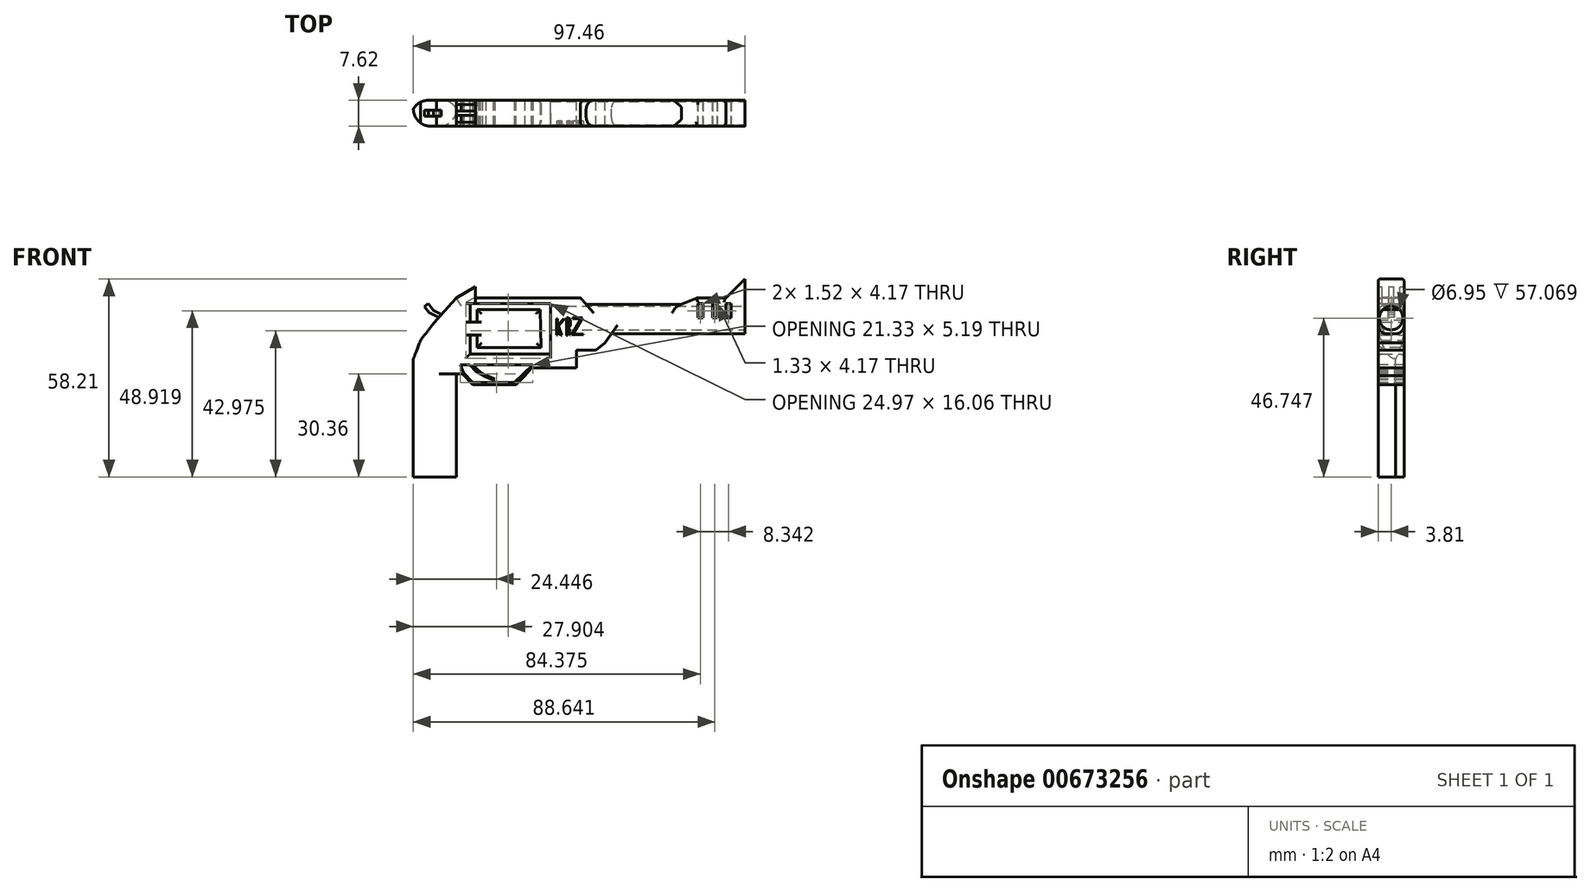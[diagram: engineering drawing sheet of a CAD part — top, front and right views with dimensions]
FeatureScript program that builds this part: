
annotation { "Feature Type Name" : "Feature", "Feature Type Description" : "" }
export const myFeature = defineFeature(function(context is Context, id is Id, definition is map)
    precondition{}
    {
        {
            var Q0;
            Q0=qCreatedBy(makeId("Front.planeOp"),FACE);
            var sketch = newSketch(context, id + "F0", { "sketchPlane" : qUnion([Q0])});
            skLineSegment(sketch, "E0", {"start": v(-48.06, -27.2) * mm, "end": v(-48.06, 3.13) * mm});
            skLineSegment(sketch, "E1", {"start": v(-48.06, 3.13) * mm, "end": v(-46.36, 3.13) * mm});
            skLineSegment(sketch, "E2", {"start": v(-46.36, 3.13) * mm, "end": v(-43.32, 0) * mm});
            skLineSegment(sketch, "E3", {"start": v(-43.32, 0) * mm, "end": v(-38.77, 0) * mm});
            skLineSegment(sketch, "E4", {"start": v(-38.77, 0) * mm, "end": v(-30.62, 0) * mm});
            skLineSegment(sketch, "E5", {"start": v(-30.62, 0) * mm, "end": v(-27.97, 2.56) * mm});
            skLineSegment(sketch, "E6", {"start": v(-27.97, 2.56) * mm, "end": v(-26.07, 4.83) * mm});
            skLineSegment(sketch, "E7", {"start": v(-26.07, 4.83) * mm, "end": v(-12.8, 4.83) * mm});
            skLineSegment(sketch, "E8", {"start": v(-12.8, 4.83) * mm, "end": v(-12.8, 10.14) * mm});
            skLineSegment(sketch, "E9", {"start": v(-12.8, 10.14) * mm, "end": v(-10.52, 10.14) * mm});
            skLineSegment(sketch, "E10", {"start": v(-10.52, 10.14) * mm, "end": v(-7.1, 10.14) * mm});
            skLineSegment(sketch, "E11", {"start": v(-7.1, 10.14) * mm, "end": v(-4.46, 12.23) * mm});
            skLineSegment(sketch, "E12", {"start": v(-4.46, 12.23) * mm, "end": v(-2.56, 14.88) * mm});
            skLineSegment(sketch, "E13", {"start": v(-2.56, 14.88) * mm, "end": v(4.83, 14.88) * mm});
            skLineSegment(sketch, "E14", {"start": v(4.83, 14.88) * mm, "end": v(14.88, 14.88) * mm});
            skLineSegment(sketch, "E15", {"start": v(14.88, 14.88) * mm, "end": v(23.8, 14.88) * mm});
            skLineSegment(sketch, "E16", {"start": v(23.8, 14.88) * mm, "end": v(30.8, 14.88) * mm});
            skLineSegment(sketch, "E17", {"start": v(30.8, 14.88) * mm, "end": v(36.69, 14.88) * mm});
            skLineSegment(sketch, "E18", {"start": v(36.69, 14.88) * mm, "end": v(36.69, 25.5) * mm});
            skLineSegment(sketch, "E19", {"start": v(36.69, 25.5) * mm, "end": v(36.69, 31) * mm});
            skLineSegment(sketch, "E20", {"start": v(36.69, 31) * mm, "end": v(31.19, 25.5) * mm});
            skLineSegment(sketch, "E21", {"start": v(31.19, 25.5) * mm, "end": v(22.66, 25.5) * mm});
            skLineSegment(sketch, "E22", {"start": v(22.66, 25.5) * mm, "end": v(18.1, 23.6) * mm});
            skLineSegment(sketch, "E23", {"start": v(18.1, 23.6) * mm, "end": v(12.04, 23.6) * mm});
            skLineSegment(sketch, "E24", {"start": v(12.04, 23.6) * mm, "end": v(-9.95, 23.6) * mm});
            skLineSegment(sketch, "E25", {"start": v(-9.95, 23.6) * mm, "end": v(-11.66, 25.5) * mm});
            skLineSegment(sketch, "E26", {"start": v(-11.66, 25.5) * mm, "end": v(-24.55, 25.5) * mm});
            skLineSegment(sketch, "E27", {"start": v(-24.55, 25.5) * mm, "end": v(-42.56, 25.5) * mm});
            skLineSegment(sketch, "E28", {"start": v(-53.75, 29.1) * mm, "end": v(-56.78, 29.1) * mm});
            skLineSegment(sketch, "E29", {"start": v(-48.06, -27.2) * mm, "end": v(-60.77, -27.2) * mm});
            skLineSegment(sketch, "E30", {"start": v(-60.77, -27.2) * mm, "end": v(-60.77, 7.49) * mm});
            skLineSegment(sketch, "E31", {"start": v(-60.77, 7.49) * mm, "end": v(-58.68, 12.99) * mm});
            skLineSegment(sketch, "E32", {"start": v(-58.68, 12.99) * mm, "end": v(-53.94, 19.05) * mm});
            skLineSegment(sketch, "E33", {"start": v(-53.94, 19.05) * mm, "end": v(-48.06, 25.5) * mm});
            skLineSegment(sketch, "E34", {"start": v(-42.56, 25.5) * mm, "end": v(-42.56, 28.72) * mm});
            skLineSegment(sketch, "E35", {"start": v(-42.56, 28.72) * mm, "end": v(-48.06, 25.5) * mm});
            skLineSegment(sketch, "E36.bottom", {"start": v(22.85, 23.8) * mm, "end": v(24.36, 23.8) * mm});
            skLineSegment(sketch, "E36.top", {"start": v(22.85, 19.62) * mm, "end": v(24.36, 19.62) * mm});
            skLineSegment(sketch, "E36.left", {"start": v(22.85, 23.8) * mm, "end": v(22.85, 19.62) * mm});
            skLineSegment(sketch, "E36.right", {"start": v(24.36, 23.8) * mm, "end": v(24.36, 19.62) * mm});
            skLineSegment(sketch, "E37.bottom", {"start": v(27.2, 23.8) * mm, "end": v(28.53, 23.8) * mm});
            skLineSegment(sketch, "E37.top", {"start": v(27.2, 19.62) * mm, "end": v(28.53, 19.62) * mm});
            skLineSegment(sketch, "E37.left", {"start": v(27.2, 23.8) * mm, "end": v(27.2, 19.62) * mm});
            skLineSegment(sketch, "E37.right", {"start": v(28.53, 23.8) * mm, "end": v(28.53, 19.62) * mm});
            skLineSegment(sketch, "E38.bottom", {"start": v(31.19, 23.8) * mm, "end": v(32.7, 23.8) * mm});
            skLineSegment(sketch, "E38.top", {"start": v(31.19, 19.62) * mm, "end": v(32.7, 19.62) * mm});
            skLineSegment(sketch, "E38.left", {"start": v(31.19, 23.8) * mm, "end": v(31.19, 19.62) * mm});
            skLineSegment(sketch, "E38.right", {"start": v(32.7, 23.8) * mm, "end": v(32.7, 19.62) * mm});
            skLineSegment(sketch, "E39", {"start": v(-42, 22.28) * mm, "end": v(-42, 10.9) * mm});
            skPoint(sketch, "E39.startSnap0", {"position": v(-51, 22.28) * mm});
            skLineSegment(sketch, "E40", {"start": v(-42, 10.9) * mm, "end": v(-22.47, 10.9) * mm});
            skLineSegment(sketch, "E41", {"start": v(-22.47, 10.9) * mm, "end": v(-22.47, 22.28) * mm});
            skLineSegment(sketch, "E42", {"start": v(-22.47, 22.28) * mm, "end": v(-42, 22.28) * mm});
            skLineSegment(sketch, "E43", {"start": v(-42, 22.28) * mm, "end": v(-44.08, 22.28) * mm});
            skLineSegment(sketch, "E44", {"start": v(-44.08, 22.28) * mm, "end": v(-44.08, 18.3) * mm});
            skLineSegment(sketch, "E45", {"start": v(-44.08, 18.3) * mm, "end": v(-42, 18.3) * mm});
            skLineSegment(sketch, "E46", {"start": v(-42, 14.5) * mm, "end": v(-44.08, 14.5) * mm});
            skLineSegment(sketch, "E47", {"start": v(-44.08, 14.5) * mm, "end": v(-44.08, 9) * mm});
            skLineSegment(sketch, "E48", {"start": v(-44.08, 9) * mm, "end": v(-20.38, 9) * mm});
            skLineSegment(sketch, "E49", {"start": v(-20.38, 9) * mm, "end": v(-20.38, 23.8) * mm});
            skLineSegment(sketch, "E50", {"start": v(-20.38, 23.8) * mm, "end": v(-44.08, 23.8) * mm});
            skLineSegment(sketch, "E51", {"start": v(-44.08, 23.8) * mm, "end": v(-44.08, 22.28) * mm});
            skSolve(sketch);
        }
        {
            var Q0;
            Q0 = qSketchRegion(id + "F0", true);
            extrude(context, id + "F1", {"entities" : qUnion([Q0]), "depth" : 7.62 * mm, "offsetDistance" : 25.4 * mm});
        }
        {
            var Q0;
            Q0=makeQuery(id+"F1.opExtrude","CAP_FACE",FACE,{"disambiguationData":[OSD([sQuery(id+"F0.wireOp",EDGE,"E0"),sQuery(id+"F0.wireOp",EDGE,"E1"),sQuery(id+"F0.wireOp",EDGE,"E2"),sQuery(id+"F0.wireOp",EDGE,"E3"),sQuery(id+"F0.wireOp",EDGE,"E4"),sQuery(id+"F0.wireOp",EDGE,"E5"),sQuery(id+"F0.wireOp",EDGE,"E6"),sQuery(id+"F0.wireOp",EDGE,"E7"),sQuery(id+"F0.wireOp",EDGE,"E8"),sQuery(id+"F0.wireOp",EDGE,"E9"),sQuery(id+"F0.wireOp",EDGE,"E10"),sQuery(id+"F0.wireOp",EDGE,"E11"),sQuery(id+"F0.wireOp",EDGE,"E12"),sQuery(id+"F0.wireOp",EDGE,"E13"),sQuery(id+"F0.wireOp",EDGE,"E14"),sQuery(id+"F0.wireOp",EDGE,"E15"),sQuery(id+"F0.wireOp",EDGE,"E16"),sQuery(id+"F0.wireOp",EDGE,"E17"),sQuery(id+"F0.wireOp",EDGE,"E18"),sQuery(id+"F0.wireOp",EDGE,"E19"),sQuery(id+"F0.wireOp",EDGE,"E20"),sQuery(id+"F0.wireOp",EDGE,"E21"),sQuery(id+"F0.wireOp",EDGE,"E22"),sQuery(id+"F0.wireOp",EDGE,"E23"),sQuery(id+"F0.wireOp",EDGE,"E24"),sQuery(id+"F0.wireOp",EDGE,"E25"),sQuery(id+"F0.wireOp",EDGE,"E26"),sQuery(id+"F0.wireOp",EDGE,"E27"),sQuery(id+"F0.wireOp",EDGE,"E29"),sQuery(id+"F0.wireOp",EDGE,"E30"),sQuery(id+"F0.wireOp",EDGE,"E31"),sQuery(id+"F0.wireOp",EDGE,"E32"),sQuery(id+"F0.wireOp",EDGE,"E33"),sQuery(id+"F0.wireOp",EDGE,"E34"),sQuery(id+"F0.wireOp",EDGE,"E35"),sQuery(id+"F0.wireOp",EDGE,"E36.bottom"),sQuery(id+"F0.wireOp",EDGE,"E36.top"),sQuery(id+"F0.wireOp",EDGE,"E36.left"),sQuery(id+"F0.wireOp",EDGE,"E36.right"),sQuery(id+"F0.wireOp",EDGE,"E37.bottom"),sQuery(id+"F0.wireOp",EDGE,"E37.top"),sQuery(id+"F0.wireOp",EDGE,"E37.left"),sQuery(id+"F0.wireOp",EDGE,"E37.right"),sQuery(id+"F0.wireOp",EDGE,"E38.bottom"),sQuery(id+"F0.wireOp",EDGE,"E38.top"),sQuery(id+"F0.wireOp",EDGE,"E38.left"),sQuery(id+"F0.wireOp",EDGE,"E38.right"),sQuery(id+"F0.wireOp",EDGE,"E39"),sQuery(id+"F0.wireOp",EDGE,"E44"),sQuery(id+"F0.wireOp",EDGE,"E45"),sQuery(id+"F0.wireOp",EDGE,"E46"),sQuery(id+"F0.wireOp",EDGE,"E47"),sQuery(id+"F0.wireOp",EDGE,"E48"),sQuery(id+"F0.wireOp",EDGE,"E49"),sQuery(id+"F0.wireOp",EDGE,"E50"),sQuery(id+"F0.wireOp",EDGE,"E51")])],"isStart":false});
            var sketch = newSketch(context, id + "F2", { "sketchPlane" : qUnion([Q0])});
            skLineSegment(sketch, "E52", {"start": v(-42, 10.9) * mm, "end": v(-23.23, 10.9) * mm});
            skLineSegment(sketch, "E53", {"start": v(-23.42, 22.09) * mm, "end": v(-23.23, 10.9) * mm});
            skLineSegment(sketch, "E54", {"start": v(-42, 22.09) * mm, "end": v(-23.42, 22.09) * mm});
            skLineSegment(sketch, "E55", {"start": v(-42, 22.09) * mm, "end": v(-42, 21.05) * mm});
            skPoint(sketch, "E55.endSnap0", {"position": v(-44.08, 21.05) * mm});
            skLineSegment(sketch, "E56", {"start": v(-42, 21.05) * mm, "end": v(-42, 18.3) * mm});
            skLineSegment(sketch, "E57", {"start": v(-42, 18.3) * mm, "end": v(-44.08, 18.3) * mm});
            skLineSegment(sketch, "E58", {"start": v(-44.08, 18.3) * mm, "end": v(-44.08, 14.5) * mm});
            skLineSegment(sketch, "E59", {"start": v(-44.08, 14.5) * mm, "end": v(-42, 14.5) * mm});
            skLineSegment(sketch, "E60", {"start": v(-42, 14.5) * mm, "end": v(-42, 10.9) * mm});
            skSolve(sketch);
        }
        {
            var Q0;
            Q0 = qSketchRegion(id + "F2", true);
            extrude(context, id + "F3", {"entities" : qUnion([Q0]), "operationType" : NewBodyOperationType.ADD, "oppositeDirection" : true, "depth" : 7.62 * mm, "offsetDistance" : 25.4 * mm});
        }
        {
            var Q0;
            Q0=makeQuery(id+"F3.boolean.opBoolean","MERGE",FACE,{"derivedFrom":[makeQuery(id+"F1.opExtrude","CAP_FACE",FACE,{"disambiguationData":[OSD([sQuery(id+"F0.wireOp",EDGE,"E0"),sQuery(id+"F0.wireOp",EDGE,"E1"),sQuery(id+"F0.wireOp",EDGE,"E2"),sQuery(id+"F0.wireOp",EDGE,"E3"),sQuery(id+"F0.wireOp",EDGE,"E4"),sQuery(id+"F0.wireOp",EDGE,"E5"),sQuery(id+"F0.wireOp",EDGE,"E6"),sQuery(id+"F0.wireOp",EDGE,"E7"),sQuery(id+"F0.wireOp",EDGE,"E8"),sQuery(id+"F0.wireOp",EDGE,"E9"),sQuery(id+"F0.wireOp",EDGE,"E10"),sQuery(id+"F0.wireOp",EDGE,"E11"),sQuery(id+"F0.wireOp",EDGE,"E12"),sQuery(id+"F0.wireOp",EDGE,"E13"),sQuery(id+"F0.wireOp",EDGE,"E14"),sQuery(id+"F0.wireOp",EDGE,"E15"),sQuery(id+"F0.wireOp",EDGE,"E16"),sQuery(id+"F0.wireOp",EDGE,"E17"),sQuery(id+"F0.wireOp",EDGE,"E18"),sQuery(id+"F0.wireOp",EDGE,"E19"),sQuery(id+"F0.wireOp",EDGE,"E20"),sQuery(id+"F0.wireOp",EDGE,"E21"),sQuery(id+"F0.wireOp",EDGE,"E22"),sQuery(id+"F0.wireOp",EDGE,"E23"),sQuery(id+"F0.wireOp",EDGE,"E24"),sQuery(id+"F0.wireOp",EDGE,"E25"),sQuery(id+"F0.wireOp",EDGE,"E26"),sQuery(id+"F0.wireOp",EDGE,"E27"),sQuery(id+"F0.wireOp",EDGE,"E29"),sQuery(id+"F0.wireOp",EDGE,"E30"),sQuery(id+"F0.wireOp",EDGE,"E31"),sQuery(id+"F0.wireOp",EDGE,"E32"),sQuery(id+"F0.wireOp",EDGE,"E33"),sQuery(id+"F0.wireOp",EDGE,"E34"),sQuery(id+"F0.wireOp",EDGE,"E35"),sQuery(id+"F0.wireOp",EDGE,"E36.bottom"),sQuery(id+"F0.wireOp",EDGE,"E36.top"),sQuery(id+"F0.wireOp",EDGE,"E36.left"),sQuery(id+"F0.wireOp",EDGE,"E36.right"),sQuery(id+"F0.wireOp",EDGE,"E37.bottom"),sQuery(id+"F0.wireOp",EDGE,"E37.top"),sQuery(id+"F0.wireOp",EDGE,"E37.left"),sQuery(id+"F0.wireOp",EDGE,"E37.right"),sQuery(id+"F0.wireOp",EDGE,"E38.bottom"),sQuery(id+"F0.wireOp",EDGE,"E38.top"),sQuery(id+"F0.wireOp",EDGE,"E38.left"),sQuery(id+"F0.wireOp",EDGE,"E38.right"),sQuery(id+"F0.wireOp",EDGE,"E39"),sQuery(id+"F0.wireOp",EDGE,"E44"),sQuery(id+"F0.wireOp",EDGE,"E45"),sQuery(id+"F0.wireOp",EDGE,"E46"),sQuery(id+"F0.wireOp",EDGE,"E47"),sQuery(id+"F0.wireOp",EDGE,"E48"),sQuery(id+"F0.wireOp",EDGE,"E49"),sQuery(id+"F0.wireOp",EDGE,"E50"),sQuery(id+"F0.wireOp",EDGE,"E51")])],"isStart":false}),makeQuery(id+"F3.opExtrude","CAP_FACE",FACE,{"disambiguationData":[OSD([sQuery(id+"F2.wireOp",EDGE,"E52"),sQuery(id+"F2.wireOp",EDGE,"E53"),sQuery(id+"F2.wireOp",EDGE,"E54"),sQuery(id+"F2.wireOp",EDGE,"E55"),sQuery(id+"F2.wireOp",EDGE,"E56"),sQuery(id+"F2.wireOp",EDGE,"E57"),sQuery(id+"F2.wireOp",EDGE,"E58"),sQuery(id+"F2.wireOp",EDGE,"E59"),sQuery(id+"F2.wireOp",EDGE,"E60")])],"isStart":true})]});
            var sketch = newSketch(context, id + "F4", { "sketchPlane" : qUnion([Q0])});
            skLineSegment(sketch, "E61", {"start": v(-46, 3.4) * mm, "end": v(-43.23, 0.55) * mm});
            skLineSegment(sketch, "E62", {"start": v(-43.23, 0.55) * mm, "end": v(-31.05, 0.55) * mm});
            skLineSegment(sketch, "E63", {"start": v(-31.05, 0.55) * mm, "end": v(-25.66, 5.75) * mm});
            skLineSegment(sketch, "E64", {"start": v(-46.99, 5.75) * mm, "end": v(-46, 3.4) * mm});
            skLineSegment(sketch, "E65", {"start": v(-44.12, 5.75) * mm, "end": v(-43.73, 5.34) * mm});
            skLineSegment(sketch, "E66", {"start": v(-43.73, 5.34) * mm, "end": v(-43.23, 4.83) * mm});
            skLineSegment(sketch, "E67", {"start": v(-43.23, 4.83) * mm, "end": v(-42.22, 3.8) * mm});
            skLineSegment(sketch, "E68", {"start": v(-42.22, 3.8) * mm, "end": v(-41.17, 3.13) * mm});
            skLineSegment(sketch, "E69", {"start": v(-41.17, 3.13) * mm, "end": v(-39.42, 2.2) * mm});
            skLineSegment(sketch, "E70", {"start": v(-39.42, 2.2) * mm, "end": v(-37.34, 1.3) * mm});
            skLineSegment(sketch, "E71", {"start": v(-37.34, 1.3) * mm, "end": v(-36.79, 1.61) * mm});
            skLineSegment(sketch, "E72", {"start": v(-36.79, 1.61) * mm, "end": v(-38.84, 2.52) * mm});
            skLineSegment(sketch, "E73", {"start": v(-38.84, 2.52) * mm, "end": v(-40.5, 3.26) * mm});
            skLineSegment(sketch, "E74", {"start": v(-40.5, 3.26) * mm, "end": v(-41.6, 4.16) * mm});
            skLineSegment(sketch, "E75", {"start": v(-41.6, 4.16) * mm, "end": v(-42.44, 4.92) * mm});
            skLineSegment(sketch, "E76", {"start": v(-42.44, 4.92) * mm, "end": v(-43, 5.75) * mm});
            skLineSegment(sketch, "E77", {"start": v(-46.99, 5.75) * mm, "end": v(-44.12, 5.75) * mm});
            skLineSegment(sketch, "E78", {"start": v(-43, 5.75) * mm, "end": v(-25.66, 5.75) * mm});
            skSolve(sketch);
        }
        {
            var Q0;
            Q0 = qSketchRegion(id + "F4", true);
            extrude(context, id + "F5", {"entities" : qUnion([Q0]), "operationType" : NewBodyOperationType.REMOVE, "oppositeDirection" : true, "depth" : 25.4 * mm, "offsetDistance" : 25.4 * mm});
        }
        {
            var Q0;
            Q0=makeQuery(id+"F1.opExtrude","SWEPT_FACE",FACE,{"disambiguationData":[OSD([sQuery(id+"F0.wireOp",EDGE,"E18"),sQuery(id+"F0.wireOp",EDGE,"E19")])]});
            var sketch = newSketch(context, id + "F6", { "sketchPlane" : qUnion([Q0])});
            skCircle(sketch, "E79", {"center": v(-3.81, 19.54) * mm, "radius": 3.47 * mm});
            skPoint(sketch, "E79.centerSnap0", {"position": v(-3.81, 14.88) * mm});
            skSolve(sketch);
        }
        {
            var Q0;
            Q0 = qSketchRegion(id + "F6", true);
            extrude(context, id + "F7", {"entities" : qUnion([Q0]), "operationType" : NewBodyOperationType.REMOVE, "oppositeDirection" : true, "depth" : 57.9 * mm, "offsetDistance" : 25.4 * mm});
        }
        {
            var Q0;
            Q0=makeQuery(id+"F1.opExtrude","CAP_EDGE",EDGE,{"disambiguationData":[OSD([sQuery(id+"F0.wireOp",EDGE,"E13"),sQuery(id+"F0.wireOp",EDGE,"E14"),sQuery(id+"F0.wireOp",EDGE,"E15"),sQuery(id+"F0.wireOp",EDGE,"E16"),sQuery(id+"F0.wireOp",EDGE,"E17")])],"isStart":false});
            fillet(context, id + "F8", {"entities" : qUnion([Q0]), "radius" : 2.54 * mm, "tangentPropagation" : true, "allowEdgeOverflow" : false});
        }
        {
            var Q0;
            Q0=makeQuery(id+"F1.opExtrude","CAP_EDGE",EDGE,{"disambiguationData":[OSD([sQuery(id+"F0.wireOp",EDGE,"E13"),sQuery(id+"F0.wireOp",EDGE,"E14"),sQuery(id+"F0.wireOp",EDGE,"E15"),sQuery(id+"F0.wireOp",EDGE,"E16"),sQuery(id+"F0.wireOp",EDGE,"E17")])],"isStart":true});
            fillet(context, id + "F9", {"entities" : qUnion([Q0]), "radius" : 2.54 * mm, "tangentPropagation" : true, "allowEdgeOverflow" : false});
        }
        {
            var Q0;
            Q0=makeQuery(id+"F1.opExtrude","CAP_EDGE",EDGE,{"disambiguationData":[OSD([sQuery(id+"F0.wireOp",EDGE,"E23"),sQuery(id+"F0.wireOp",EDGE,"E24")])],"isStart":false});
            fillet(context, id + "F10", {"entities" : qUnion([Q0]), "radius" : 2.54 * mm, "tangentPropagation" : true, "allowEdgeOverflow" : false});
        }
        {
            var Q0;
            Q0=makeQuery(id+"F1.opExtrude","CAP_EDGE",EDGE,{"disambiguationData":[OSD([sQuery(id+"F0.wireOp",EDGE,"E22")])],"isStart":false});
            fillet(context, id + "F11", {"entities" : qUnion([Q0]), "radius" : 1.27 * mm, "tangentPropagation" : true, "allowEdgeOverflow" : false});
        }
        {
            var Q0;
            Q0=makeQuery(id+"F1.opExtrude","CAP_EDGE",EDGE,{"disambiguationData":[OSD([sQuery(id+"F0.wireOp",EDGE,"E21")])],"isStart":true});
            fillet(context, id + "F12", {"entities" : qUnion([Q0]), "radius" : 1.27 * mm, "tangentPropagation" : true, "allowEdgeOverflow" : false});
        }
        {
            var Q0;
            Q0=makeQuery(id+"F1.opExtrude","CAP_EDGE",EDGE,{"disambiguationData":[OSD([sQuery(id+"F0.wireOp",EDGE,"E23"),sQuery(id+"F0.wireOp",EDGE,"E24")])],"isStart":true});
            fillet(context, id + "F13", {"entities" : qUnion([Q0]), "radius" : 2.54 * mm, "tangentPropagation" : true, "allowEdgeOverflow" : false});
        }
        {
            var Q0;
            Q0=makeQuery(id+"F1.opExtrude","CAP_EDGE",EDGE,{"disambiguationData":[OSD([sQuery(id+"F0.wireOp",EDGE,"E22")])],"isStart":true});
            fillet(context, id + "F14", {"entities" : qUnion([Q0]), "radius" : 1.27 * mm, "tangentPropagation" : true, "allowEdgeOverflow" : false});
        }
        {
            var Q0;
            Q0=makeQuery(id+"F1.opExtrude","SWEPT_FACE",FACE,{"disambiguationData":[OSD([sQuery(id+"F0.wireOp",EDGE,"E20")])]});
            var sketch = newSketch(context, id + "F15", { "sketchPlane" : qUnion([Q0])});
            skLineSegment(sketch, "E80", {"start": v(47.86, -1.47) * mm, "end": v(44.62, -1.47) * mm});
            skLineSegment(sketch, "E81", {"start": v(44.62, -1.47) * mm, "end": v(44.62, -3.23) * mm});
            skLineSegment(sketch, "E82", {"start": v(44.62, -3.23) * mm, "end": v(47.86, -3.23) * mm});
            skLineSegment(sketch, "E83", {"start": v(47.86, -4.5) * mm, "end": v(44.62, -4.5) * mm});
            skLineSegment(sketch, "E84", {"start": v(44.62, -4.5) * mm, "end": v(44.62, -6.58) * mm});
            skLineSegment(sketch, "E85", {"start": v(44.62, -6.58) * mm, "end": v(47.86, -6.58) * mm});
            skLineSegment(sketch, "E86", {"start": v(47.86, -6.58) * mm, "end": v(47.86, -4.5) * mm});
            skSolve(sketch);
        }
        {
            var Q0;
            Q0 = qSketchRegion(id + "F15", true);
            var Q1;
            {var subQ0=sQuery(id+"F15.wireOp",EDGE,"E80");Q1=makeQuery(id+"F15.imprint","IMPRINT",FACE,{"disambiguationData":[TD([[makeQuery(id+"F15.imprint","IMPRINT",EDGE,{"derivedFrom":subQ0}),1.0]])]});}
            extrude(context, id + "F16", {"entities" : qUnion([Q0, Q1]), "operationType" : NewBodyOperationType.REMOVE, "oppositeDirection" : true, "depth" : 25.4 * mm, "offsetDistance" : 25.4 * mm});
        }
        {
            var Q0;
            Q0=makeQuery(id+"F1.opExtrude","SWEPT_FACE",FACE,{"disambiguationData":[OSD([sQuery(id+"F0.wireOp",EDGE,"E35")])]});
            var sketch = newSketch(context, id + "F17", { "sketchPlane" : qUnion([Q0])});
            skLineSegment(sketch, "E87", {"start": v(-22.2, -3.16) * mm, "end": v(-28.57, -3.16) * mm});
            skLineSegment(sketch, "E88", {"start": v(-28.57, -3.16) * mm, "end": v(-28.57, -1.3) * mm});
            skLineSegment(sketch, "E89", {"start": v(-28.57, -1.3) * mm, "end": v(-22.2, -1.3) * mm});
            skLineSegment(sketch, "E90", {"start": v(-22.2, -1.3) * mm, "end": v(-22.2, -3.16) * mm});
            skLineSegment(sketch, "E91", {"start": v(-22.2, -4.49) * mm, "end": v(-28.57, -4.49) * mm});
            skLineSegment(sketch, "E92", {"start": v(-28.57, -4.49) * mm, "end": v(-28.57, -6.5) * mm});
            skLineSegment(sketch, "E93", {"start": v(-28.57, -6.5) * mm, "end": v(-22.2, -6.5) * mm});
            skLineSegment(sketch, "E94", {"start": v(-22.2, -6.5) * mm, "end": v(-22.2, -4.49) * mm});
            skSolve(sketch);
        }
        {
            var Q0;
            Q0 = qSketchRegion(id + "F17", true);
            extrude(context, id + "F18", {"entities" : qUnion([Q0]), "operationType" : NewBodyOperationType.REMOVE, "oppositeDirection" : true, "depth" : 2.62 * mm, "offsetDistance" : 25.4 * mm});
        }
        {
            var Q0;
            Q0=makeQuery(id+"F1.opExtrude","CAP_EDGE",EDGE,{"disambiguationData":[OSD([sQuery(id+"F0.wireOp",EDGE,"E30")])],"isStart":false});
            fillet(context, id + "F19", {"entities" : qUnion([Q0]), "radius" : 5.08 * mm, "tangentPropagation" : true, "allowEdgeOverflow" : false});
        }
        {
            var Q0;
            Q0=makeQuery(id+"F1.opExtrude","CAP_EDGE",EDGE,{"disambiguationData":[OSD([sQuery(id+"F0.wireOp",EDGE,"E0")])],"isStart":false});
            fillet(context, id + "F20", {"entities" : qUnion([Q0]), "radius" : 5.08 * mm, "tangentPropagation" : true, "allowEdgeOverflow" : false});
        }
        {
            var Q0;
            Q0=makeQuery(id+"F1.opExtrude","CAP_EDGE",EDGE,{"disambiguationData":[OSD([sQuery(id+"F0.wireOp",EDGE,"E0")])],"isStart":true});
            fillet(context, id + "F21", {"entities" : qUnion([Q0]), "radius" : 5.08 * mm, "tangentPropagation" : true, "allowEdgeOverflow" : false});
        }
        {
            var Q0;
            Q0=makeQuery(id+"F1.opExtrude","CAP_EDGE",EDGE,{"disambiguationData":[OSD([sQuery(id+"F0.wireOp",EDGE,"E30")])],"isStart":true});
            fillet(context, id + "F22", {"entities" : qUnion([Q0]), "radius" : 5.08 * mm, "tangentPropagation" : true, "allowEdgeOverflow" : false});
        }
        {
            var Q0;
            Q0=makeQuery(id+"F3.boolean.opBoolean","MERGE",FACE,{"derivedFrom":[makeQuery(id+"F1.opExtrude","CAP_FACE",FACE,{"disambiguationData":[OSD([sQuery(id+"F0.wireOp",EDGE,"E0"),sQuery(id+"F0.wireOp",EDGE,"E1"),sQuery(id+"F0.wireOp",EDGE,"E2"),sQuery(id+"F0.wireOp",EDGE,"E3"),sQuery(id+"F0.wireOp",EDGE,"E4"),sQuery(id+"F0.wireOp",EDGE,"E5"),sQuery(id+"F0.wireOp",EDGE,"E6"),sQuery(id+"F0.wireOp",EDGE,"E7"),sQuery(id+"F0.wireOp",EDGE,"E8"),sQuery(id+"F0.wireOp",EDGE,"E9"),sQuery(id+"F0.wireOp",EDGE,"E10"),sQuery(id+"F0.wireOp",EDGE,"E11"),sQuery(id+"F0.wireOp",EDGE,"E12"),sQuery(id+"F0.wireOp",EDGE,"E13"),sQuery(id+"F0.wireOp",EDGE,"E14"),sQuery(id+"F0.wireOp",EDGE,"E15"),sQuery(id+"F0.wireOp",EDGE,"E16"),sQuery(id+"F0.wireOp",EDGE,"E17"),sQuery(id+"F0.wireOp",EDGE,"E18"),sQuery(id+"F0.wireOp",EDGE,"E19"),sQuery(id+"F0.wireOp",EDGE,"E20"),sQuery(id+"F0.wireOp",EDGE,"E21"),sQuery(id+"F0.wireOp",EDGE,"E22"),sQuery(id+"F0.wireOp",EDGE,"E23"),sQuery(id+"F0.wireOp",EDGE,"E24"),sQuery(id+"F0.wireOp",EDGE,"E25"),sQuery(id+"F0.wireOp",EDGE,"E26"),sQuery(id+"F0.wireOp",EDGE,"E27"),sQuery(id+"F0.wireOp",EDGE,"E29"),sQuery(id+"F0.wireOp",EDGE,"E30"),sQuery(id+"F0.wireOp",EDGE,"E31"),sQuery(id+"F0.wireOp",EDGE,"E32"),sQuery(id+"F0.wireOp",EDGE,"E33"),sQuery(id+"F0.wireOp",EDGE,"E34"),sQuery(id+"F0.wireOp",EDGE,"E35"),sQuery(id+"F0.wireOp",EDGE,"E36.bottom"),sQuery(id+"F0.wireOp",EDGE,"E36.top"),sQuery(id+"F0.wireOp",EDGE,"E36.left"),sQuery(id+"F0.wireOp",EDGE,"E36.right"),sQuery(id+"F0.wireOp",EDGE,"E37.bottom"),sQuery(id+"F0.wireOp",EDGE,"E37.top"),sQuery(id+"F0.wireOp",EDGE,"E37.left"),sQuery(id+"F0.wireOp",EDGE,"E37.right"),sQuery(id+"F0.wireOp",EDGE,"E38.bottom"),sQuery(id+"F0.wireOp",EDGE,"E38.top"),sQuery(id+"F0.wireOp",EDGE,"E38.left"),sQuery(id+"F0.wireOp",EDGE,"E38.right"),sQuery(id+"F0.wireOp",EDGE,"E39"),sQuery(id+"F0.wireOp",EDGE,"E44"),sQuery(id+"F0.wireOp",EDGE,"E45"),sQuery(id+"F0.wireOp",EDGE,"E46"),sQuery(id+"F0.wireOp",EDGE,"E47"),sQuery(id+"F0.wireOp",EDGE,"E48"),sQuery(id+"F0.wireOp",EDGE,"E49"),sQuery(id+"F0.wireOp",EDGE,"E50"),sQuery(id+"F0.wireOp",EDGE,"E51")])],"isStart":false}),makeQuery(id+"F3.opExtrude","CAP_FACE",FACE,{"disambiguationData":[OSD([sQuery(id+"F2.wireOp",EDGE,"E52"),sQuery(id+"F2.wireOp",EDGE,"E53"),sQuery(id+"F2.wireOp",EDGE,"E54"),sQuery(id+"F2.wireOp",EDGE,"E55"),sQuery(id+"F2.wireOp",EDGE,"E56"),sQuery(id+"F2.wireOp",EDGE,"E57"),sQuery(id+"F2.wireOp",EDGE,"E58"),sQuery(id+"F2.wireOp",EDGE,"E59"),sQuery(id+"F2.wireOp",EDGE,"E60")])],"isStart":true})]});
            var sketch = newSketch(context, id + "F23", { "sketchPlane" : qUnion([Q0])});
            skLineSegment(sketch, "E95", {"start": v(-51.58, 20.16) * mm, "end": v(-54.85, 21.85) * mm});
            skLineSegment(sketch, "E96", {"start": v(-54.85, 21.85) * mm, "end": v(-56.42, 23.76) * mm});
            skLineSegment(sketch, "E97", {"start": v(-56.42, 23.76) * mm, "end": v(-57.52, 22.87) * mm});
            skLineSegment(sketch, "E98", {"start": v(-57.52, 22.87) * mm, "end": v(-56.06, 21.1) * mm});
            skLineSegment(sketch, "E99", {"start": v(-56.06, 21.1) * mm, "end": v(-52.14, 19.14) * mm});
            skLineSegment(sketch, "E100", {"start": v(-52.14, 19.14) * mm, "end": v(-51.58, 20.16) * mm});
            skSolve(sketch);
        }
        {
            var Q0;
            Q0 = qSketchRegion(id + "F23", true);
            extrude(context, id + "F24", {"entities" : qUnion([Q0]), "operationType" : NewBodyOperationType.ADD, "oppositeDirection" : true, "depth" : 4.72 * mm, "offsetDistance" : 25.4 * mm});
        }
        {
            var Q0;
            Q0=makeQuery(id+"F24.boolean.opBoolean","MERGE",FACE,{"derivedFrom":[makeQuery(id+"F3.boolean.opBoolean","MERGE",FACE,{"derivedFrom":[makeQuery(id+"F1.opExtrude","CAP_FACE",FACE,{"disambiguationData":[OSD([sQuery(id+"F0.wireOp",EDGE,"E0"),sQuery(id+"F0.wireOp",EDGE,"E1"),sQuery(id+"F0.wireOp",EDGE,"E2"),sQuery(id+"F0.wireOp",EDGE,"E3"),sQuery(id+"F0.wireOp",EDGE,"E4"),sQuery(id+"F0.wireOp",EDGE,"E5"),sQuery(id+"F0.wireOp",EDGE,"E6"),sQuery(id+"F0.wireOp",EDGE,"E7"),sQuery(id+"F0.wireOp",EDGE,"E8"),sQuery(id+"F0.wireOp",EDGE,"E9"),sQuery(id+"F0.wireOp",EDGE,"E10"),sQuery(id+"F0.wireOp",EDGE,"E11"),sQuery(id+"F0.wireOp",EDGE,"E12"),sQuery(id+"F0.wireOp",EDGE,"E13"),sQuery(id+"F0.wireOp",EDGE,"E14"),sQuery(id+"F0.wireOp",EDGE,"E15"),sQuery(id+"F0.wireOp",EDGE,"E16"),sQuery(id+"F0.wireOp",EDGE,"E17"),sQuery(id+"F0.wireOp",EDGE,"E18"),sQuery(id+"F0.wireOp",EDGE,"E19"),sQuery(id+"F0.wireOp",EDGE,"E20"),sQuery(id+"F0.wireOp",EDGE,"E21"),sQuery(id+"F0.wireOp",EDGE,"E22"),sQuery(id+"F0.wireOp",EDGE,"E23"),sQuery(id+"F0.wireOp",EDGE,"E24"),sQuery(id+"F0.wireOp",EDGE,"E25"),sQuery(id+"F0.wireOp",EDGE,"E26"),sQuery(id+"F0.wireOp",EDGE,"E27"),sQuery(id+"F0.wireOp",EDGE,"E29"),sQuery(id+"F0.wireOp",EDGE,"E30"),sQuery(id+"F0.wireOp",EDGE,"E31"),sQuery(id+"F0.wireOp",EDGE,"E32"),sQuery(id+"F0.wireOp",EDGE,"E33"),sQuery(id+"F0.wireOp",EDGE,"E34"),sQuery(id+"F0.wireOp",EDGE,"E35"),sQuery(id+"F0.wireOp",EDGE,"E36.bottom"),sQuery(id+"F0.wireOp",EDGE,"E36.top"),sQuery(id+"F0.wireOp",EDGE,"E36.left"),sQuery(id+"F0.wireOp",EDGE,"E36.right"),sQuery(id+"F0.wireOp",EDGE,"E37.bottom"),sQuery(id+"F0.wireOp",EDGE,"E37.top"),sQuery(id+"F0.wireOp",EDGE,"E37.left"),sQuery(id+"F0.wireOp",EDGE,"E37.right"),sQuery(id+"F0.wireOp",EDGE,"E38.bottom"),sQuery(id+"F0.wireOp",EDGE,"E38.top"),sQuery(id+"F0.wireOp",EDGE,"E38.left"),sQuery(id+"F0.wireOp",EDGE,"E38.right"),sQuery(id+"F0.wireOp",EDGE,"E39"),sQuery(id+"F0.wireOp",EDGE,"E44"),sQuery(id+"F0.wireOp",EDGE,"E45"),sQuery(id+"F0.wireOp",EDGE,"E46"),sQuery(id+"F0.wireOp",EDGE,"E47"),sQuery(id+"F0.wireOp",EDGE,"E48"),sQuery(id+"F0.wireOp",EDGE,"E49"),sQuery(id+"F0.wireOp",EDGE,"E50"),sQuery(id+"F0.wireOp",EDGE,"E51")])],"isStart":false}),makeQuery(id+"F3.opExtrude","CAP_FACE",FACE,{"disambiguationData":[OSD([sQuery(id+"F2.wireOp",EDGE,"E52"),sQuery(id+"F2.wireOp",EDGE,"E53"),sQuery(id+"F2.wireOp",EDGE,"E54"),sQuery(id+"F2.wireOp",EDGE,"E55"),sQuery(id+"F2.wireOp",EDGE,"E56"),sQuery(id+"F2.wireOp",EDGE,"E57"),sQuery(id+"F2.wireOp",EDGE,"E58"),sQuery(id+"F2.wireOp",EDGE,"E59"),sQuery(id+"F2.wireOp",EDGE,"E60")])],"isStart":true})]}),makeQuery(id+"F24.opExtrude","CAP_FACE",FACE,{"disambiguationData":[OSD([sQuery(id+"F23.wireOp",EDGE,"E95"),sQuery(id+"F23.wireOp",EDGE,"E96"),sQuery(id+"F23.wireOp",EDGE,"E97"),sQuery(id+"F23.wireOp",EDGE,"E98"),sQuery(id+"F23.wireOp",EDGE,"E99"),sQuery(id+"F23.wireOp",EDGE,"E100")])],"isStart":true})]});
            var sketch = newSketch(context, id + "F25", { "sketchPlane" : qUnion([Q0])});
            skLineSegment(sketch, "E101", {"start": v(-51.03, 22.25) * mm, "end": v(-54.97, 17.92) * mm});
            skLineSegment(sketch, "E102", {"start": v(-54.97, 17.92) * mm, "end": v(-60.83, 23.76) * mm});
            skLineSegment(sketch, "E103", {"start": v(-60.83, 23.76) * mm, "end": v(-54.9, 24.92) * mm});
            skLineSegment(sketch, "E104", {"start": v(-54.9, 24.92) * mm, "end": v(-51.03, 22.25) * mm});
            skSolve(sketch);
        }
        {
            var Q0;
            Q0 = qSketchRegion(id + "F25", true);
            extrude(context, id + "F26", {"entities" : qUnion([Q0]), "operationType" : NewBodyOperationType.REMOVE, "oppositeDirection" : true, "depth" : 3 * mm, "offsetDistance" : 25.4 * mm});
        }
        {
            var Q0;
            Q0=makeQuery(id+"F1.opExtrude","CAP_EDGE",EDGE,{"disambiguationData":[OSD([sQuery(id+"F0.wireOp",EDGE,"E26"),sQuery(id+"F0.wireOp",EDGE,"E27")])],"isStart":false});
            fillet(context, id + "F27", {"entities" : qUnion([Q0]), "radius" : 1.27 * mm, "tangentPropagation" : true, "allowEdgeOverflow" : false});
        }
        {
            var Q0;
            Q0=makeQuery(id+"F3.opExtrude","CAP_EDGE",EDGE,{"disambiguationData":[OSD([sQuery(id+"F2.wireOp",EDGE,"E54")])],"isStart":true});
            var Q1;
            Q1=makeQuery(id+"F3.opExtrude","CAP_EDGE",EDGE,{"disambiguationData":[OSD([sQuery(id+"F2.wireOp",EDGE,"E53")])],"isStart":true});
            var Q2;
            Q2=makeQuery(id+"F3.opExtrude","CAP_EDGE",EDGE,{"disambiguationData":[OSD([sQuery(id+"F2.wireOp",EDGE,"E52")])],"isStart":true});
            var Q3;
            Q3=makeQuery(id+"F3.opExtrude","CAP_EDGE",EDGE,{"disambiguationData":[OSD([sQuery(id+"F2.wireOp",EDGE,"E60")])],"isStart":true});
            var Q4;
            Q4=makeQuery(id+"F3.opExtrude","CAP_EDGE",EDGE,{"disambiguationData":[OSD([sQuery(id+"F2.wireOp",EDGE,"E55"),sQuery(id+"F2.wireOp",EDGE,"E56")])],"isStart":true});
            fillet(context, id + "F28", {"entities" : qUnion([Q0, Q1, Q2, Q3, Q4]), "radius" : 1.27 * mm, "tangentPropagation" : true, "allowEdgeOverflow" : false});
        }
        {
            var Q0;
            Q0=makeQuery(id+"F1.opExtrude","CAP_EDGE",EDGE,{"disambiguationData":[OSD([sQuery(id+"F0.wireOp",EDGE,"E44"),sQuery(id+"F0.wireOp",EDGE,"E51")])],"isStart":false});
            var Q1;
            Q1=makeQuery(id+"F1.opExtrude","CAP_EDGE",EDGE,{"disambiguationData":[OSD([sQuery(id+"F0.wireOp",EDGE,"E47")])],"isStart":false});
            var Q2;
            Q2=makeQuery(id+"F1.opExtrude","CAP_EDGE",EDGE,{"disambiguationData":[OSD([sQuery(id+"F0.wireOp",EDGE,"E48")])],"isStart":false});
            fillet(context, id + "F29", {"entities" : qUnion([Q0, Q1, Q2]), "radius" : 1.27 * mm, "tangentPropagation" : true, "allowEdgeOverflow" : false});
        }
        {
            var Q0;
            Q0=makeQuery(id+"F3.opExtrude","CAP_EDGE",EDGE,{"disambiguationData":[OSD([sQuery(id+"F2.wireOp",EDGE,"E54")])],"isStart":false});
            var Q1;
            Q1=makeQuery(id+"F3.opExtrude","CAP_EDGE",EDGE,{"disambiguationData":[OSD([sQuery(id+"F2.wireOp",EDGE,"E53")])],"isStart":false});
            var Q2;
            Q2=makeQuery(id+"F3.opExtrude","CAP_EDGE",EDGE,{"disambiguationData":[OSD([sQuery(id+"F2.wireOp",EDGE,"E52")])],"isStart":false});
            var Q3;
            Q3=makeQuery(id+"F3.opExtrude","CAP_EDGE",EDGE,{"disambiguationData":[OSD([sQuery(id+"F2.wireOp",EDGE,"E60")])],"isStart":false});
            var Q4;
            Q4=makeQuery(id+"F3.opExtrude","CAP_EDGE",EDGE,{"disambiguationData":[OSD([sQuery(id+"F2.wireOp",EDGE,"E55"),sQuery(id+"F2.wireOp",EDGE,"E56")])],"isStart":false});
            var Q5;
            Q5=makeQuery(id+"F1.opExtrude","CAP_EDGE",EDGE,{"disambiguationData":[OSD([sQuery(id+"F0.wireOp",EDGE,"E44"),sQuery(id+"F0.wireOp",EDGE,"E51")])],"isStart":true});
            var Q6;
            Q6=makeQuery(id+"F1.opExtrude","CAP_EDGE",EDGE,{"disambiguationData":[OSD([sQuery(id+"F0.wireOp",EDGE,"E26"),sQuery(id+"F0.wireOp",EDGE,"E27")])],"isStart":true});
            var Q7;
            Q7=makeQuery(id+"F1.opExtrude","CAP_EDGE",EDGE,{"disambiguationData":[OSD([sQuery(id+"F0.wireOp",EDGE,"E48")])],"isStart":true});
            var Q8;
            Q8=makeQuery(id+"F1.opExtrude","CAP_EDGE",EDGE,{"disambiguationData":[OSD([sQuery(id+"F0.wireOp",EDGE,"E47")])],"isStart":true});
            fillet(context, id + "F30", {"entities" : qUnion([Q0, Q1, Q2, Q3, Q4, Q5, Q6, Q7, Q8]), "radius" : 1.27 * mm, "tangentPropagation" : true, "allowEdgeOverflow" : false});
        }
        {
            var Q0;
            Q0=makeQuery(id+"F1.opExtrude","CAP_EDGE",EDGE,{"disambiguationData":[OSD([sQuery(id+"F0.wireOp",EDGE,"E20")])],"isStart":true});
            var Q1;
            Q1=makeQuery(id+"F1.opExtrude","CAP_EDGE",EDGE,{"disambiguationData":[OSD([sQuery(id+"F0.wireOp",EDGE,"E20")])],"isStart":false});
            fillet(context, id + "F31", {"entities" : qUnion([Q0, Q1]), "radius" : 0.5 * mm, "tangentPropagation" : true, "allowEdgeOverflow" : false});
        }
        {
            var Q0;
            Q0=makeQuery(id+"F24.boolean.opBoolean","MERGE",FACE,{"derivedFrom":[makeQuery(id+"F3.boolean.opBoolean","MERGE",FACE,{"derivedFrom":[makeQuery(id+"F1.opExtrude","CAP_FACE",FACE,{"disambiguationData":[OSD([sQuery(id+"F0.wireOp",EDGE,"E0"),sQuery(id+"F0.wireOp",EDGE,"E1"),sQuery(id+"F0.wireOp",EDGE,"E2"),sQuery(id+"F0.wireOp",EDGE,"E3"),sQuery(id+"F0.wireOp",EDGE,"E4"),sQuery(id+"F0.wireOp",EDGE,"E5"),sQuery(id+"F0.wireOp",EDGE,"E6"),sQuery(id+"F0.wireOp",EDGE,"E7"),sQuery(id+"F0.wireOp",EDGE,"E8"),sQuery(id+"F0.wireOp",EDGE,"E9"),sQuery(id+"F0.wireOp",EDGE,"E10"),sQuery(id+"F0.wireOp",EDGE,"E11"),sQuery(id+"F0.wireOp",EDGE,"E12"),sQuery(id+"F0.wireOp",EDGE,"E13"),sQuery(id+"F0.wireOp",EDGE,"E14"),sQuery(id+"F0.wireOp",EDGE,"E15"),sQuery(id+"F0.wireOp",EDGE,"E16"),sQuery(id+"F0.wireOp",EDGE,"E17"),sQuery(id+"F0.wireOp",EDGE,"E18"),sQuery(id+"F0.wireOp",EDGE,"E19"),sQuery(id+"F0.wireOp",EDGE,"E20"),sQuery(id+"F0.wireOp",EDGE,"E21"),sQuery(id+"F0.wireOp",EDGE,"E22"),sQuery(id+"F0.wireOp",EDGE,"E23"),sQuery(id+"F0.wireOp",EDGE,"E24"),sQuery(id+"F0.wireOp",EDGE,"E25"),sQuery(id+"F0.wireOp",EDGE,"E26"),sQuery(id+"F0.wireOp",EDGE,"E27"),sQuery(id+"F0.wireOp",EDGE,"E29"),sQuery(id+"F0.wireOp",EDGE,"E30"),sQuery(id+"F0.wireOp",EDGE,"E31"),sQuery(id+"F0.wireOp",EDGE,"E32"),sQuery(id+"F0.wireOp",EDGE,"E33"),sQuery(id+"F0.wireOp",EDGE,"E34"),sQuery(id+"F0.wireOp",EDGE,"E35"),sQuery(id+"F0.wireOp",EDGE,"E36.bottom"),sQuery(id+"F0.wireOp",EDGE,"E36.top"),sQuery(id+"F0.wireOp",EDGE,"E36.left"),sQuery(id+"F0.wireOp",EDGE,"E36.right"),sQuery(id+"F0.wireOp",EDGE,"E37.bottom"),sQuery(id+"F0.wireOp",EDGE,"E37.top"),sQuery(id+"F0.wireOp",EDGE,"E37.left"),sQuery(id+"F0.wireOp",EDGE,"E37.right"),sQuery(id+"F0.wireOp",EDGE,"E38.bottom"),sQuery(id+"F0.wireOp",EDGE,"E38.top"),sQuery(id+"F0.wireOp",EDGE,"E38.left"),sQuery(id+"F0.wireOp",EDGE,"E38.right"),sQuery(id+"F0.wireOp",EDGE,"E39"),sQuery(id+"F0.wireOp",EDGE,"E44"),sQuery(id+"F0.wireOp",EDGE,"E45"),sQuery(id+"F0.wireOp",EDGE,"E46"),sQuery(id+"F0.wireOp",EDGE,"E47"),sQuery(id+"F0.wireOp",EDGE,"E48"),sQuery(id+"F0.wireOp",EDGE,"E49"),sQuery(id+"F0.wireOp",EDGE,"E50"),sQuery(id+"F0.wireOp",EDGE,"E51")])],"isStart":false}),makeQuery(id+"F3.opExtrude","CAP_FACE",FACE,{"disambiguationData":[OSD([sQuery(id+"F2.wireOp",EDGE,"E52"),sQuery(id+"F2.wireOp",EDGE,"E53"),sQuery(id+"F2.wireOp",EDGE,"E54"),sQuery(id+"F2.wireOp",EDGE,"E55"),sQuery(id+"F2.wireOp",EDGE,"E56"),sQuery(id+"F2.wireOp",EDGE,"E57"),sQuery(id+"F2.wireOp",EDGE,"E58"),sQuery(id+"F2.wireOp",EDGE,"E59"),sQuery(id+"F2.wireOp",EDGE,"E60")])],"isStart":true})]}),makeQuery(id+"F24.opExtrude","CAP_FACE",FACE,{"disambiguationData":[OSD([sQuery(id+"F23.wireOp",EDGE,"E95"),sQuery(id+"F23.wireOp",EDGE,"E96"),sQuery(id+"F23.wireOp",EDGE,"E97"),sQuery(id+"F23.wireOp",EDGE,"E98"),sQuery(id+"F23.wireOp",EDGE,"E99"),sQuery(id+"F23.wireOp",EDGE,"E100")])],"isStart":true})]});
            var sketch = newSketch(context, id + "F32", { "sketchPlane" : qUnion([Q0])});
            skLineSegment(sketch, "E105", {"start": v(-18.6, 19.37) * mm, "end": v(-18.6, 14.55) * mm});
            skLineSegment(sketch, "E106", {"start": v(-18.6, 14.55) * mm, "end": v(-18.38, 14.55) * mm});
            skLineSegment(sketch, "E107", {"start": v(-18.38, 14.55) * mm, "end": v(-18.38, 19.4) * mm});
            skLineSegment(sketch, "E108", {"start": v(-18.38, 19.4) * mm, "end": v(-18.6, 19.37) * mm});
            skLineSegment(sketch, "E109", {"start": v(-18.38, 17.35) * mm, "end": v(-16.5, 19.37) * mm});
            skLineSegment(sketch, "E110", {"start": v(-16.5, 19.37) * mm, "end": v(-16.32, 19.2) * mm});
            skLineSegment(sketch, "E111", {"start": v(-16.32, 19.2) * mm, "end": v(-18.38, 16.98) * mm});
            skLineSegment(sketch, "E112", {"start": v(-18.14, 17.24) * mm, "end": v(-17.18, 14.58) * mm});
            skLineSegment(sketch, "E113", {"start": v(-17.18, 14.58) * mm, "end": v(-17.45, 14.48) * mm});
            skLineSegment(sketch, "E114", {"start": v(-17.45, 14.48) * mm, "end": v(-18.38, 16.98) * mm});
            skLineSegment(sketch, "E115", {"start": v(-15.75, 19.46) * mm, "end": v(-15.75, 14.48) * mm});
            skLineSegment(sketch, "E116", {"start": v(-15.75, 14.48) * mm, "end": v(-15.45, 14.48) * mm});
            skLineSegment(sketch, "E117", {"start": v(-15.45, 14.48) * mm, "end": v(-15.45, 19.46) * mm});
            skLineSegment(sketch, "E118", {"start": v(-15.45, 19.46) * mm, "end": v(-15.75, 19.46) * mm});
            skLineSegment(sketch, "E119", {"start": v(-15.45, 19.46) * mm, "end": v(-15.15, 19.46) * mm});
            skLineSegment(sketch, "E120", {"start": v(-15.15, 19.46) * mm, "end": v(-14.9, 19.18) * mm});
            skLineSegment(sketch, "E121", {"start": v(-14.9, 19.18) * mm, "end": v(-14.73, 18.58) * mm});
            skLineSegment(sketch, "E122", {"start": v(-14.73, 18.58) * mm, "end": v(-14.73, 17.8) * mm});
            skLineSegment(sketch, "E123", {"start": v(-14.73, 17.8) * mm, "end": v(-14.73, 17.4) * mm});
            skLineSegment(sketch, "E124", {"start": v(-14.73, 17.4) * mm, "end": v(-14.97, 17.05) * mm});
            skLineSegment(sketch, "E125", {"start": v(-14.97, 17.05) * mm, "end": v(-15.45, 16.55) * mm});
            skLineSegment(sketch, "E126", {"start": v(-15.75, 19.46) * mm, "end": v(-15.75, 19.66) * mm});
            skLineSegment(sketch, "E127", {"start": v(-15.75, 19.66) * mm, "end": v(-15.18, 19.65) * mm});
            skLineSegment(sketch, "E128", {"start": v(-15.18, 19.65) * mm, "end": v(-14.8, 19.32) * mm});
            skLineSegment(sketch, "E129", {"start": v(-14.8, 19.32) * mm, "end": v(-14.58, 18.67) * mm});
            skLineSegment(sketch, "E130", {"start": v(-14.58, 18.67) * mm, "end": v(-14.58, 17.81) * mm});
            skLineSegment(sketch, "E131", {"start": v(-14.58, 17.81) * mm, "end": v(-14.58, 17.42) * mm});
            skLineSegment(sketch, "E132", {"start": v(-14.58, 17.42) * mm, "end": v(-14.87, 16.98) * mm});
            skLineSegment(sketch, "E133", {"start": v(-14.87, 16.98) * mm, "end": v(-15.45, 16.35) * mm});
            skLineSegment(sketch, "E134", {"start": v(-15.45, 16.35) * mm, "end": v(-15.45, 16.55) * mm});
            skLineSegment(sketch, "E135", {"start": v(-15.16, 16.67) * mm, "end": v(-14.58, 14.56) * mm});
            skLineSegment(sketch, "E136", {"start": v(-14.58, 14.56) * mm, "end": v(-14.73, 14.52) * mm});
            skLineSegment(sketch, "E137", {"start": v(-14.73, 14.52) * mm, "end": v(-15.28, 16.53) * mm});
            skLineSegment(sketch, "E138", {"start": v(-15.28, 16.53) * mm, "end": v(-15.16, 16.67) * mm});
            skLineSegment(sketch, "E139", {"start": v(-13.92, 19.59) * mm, "end": v(-10.98, 19.59) * mm});
            skLineSegment(sketch, "E140", {"start": v(-10.98, 19.59) * mm, "end": v(-13.88, 14.84) * mm});
            skLineSegment(sketch, "E141", {"start": v(-13.88, 14.84) * mm, "end": v(-10.78, 14.84) * mm});
            skLineSegment(sketch, "E142", {"start": v(-10.78, 14.84) * mm, "end": v(-10.78, 14.63) * mm});
            skLineSegment(sketch, "E143", {"start": v(-10.78, 14.63) * mm, "end": v(-14.22, 14.63) * mm});
            skLineSegment(sketch, "E144", {"start": v(-14.22, 14.63) * mm, "end": v(-11.39, 19.36) * mm});
            skLineSegment(sketch, "E145", {"start": v(-11.39, 19.36) * mm, "end": v(-13.94, 19.36) * mm});
            skLineSegment(sketch, "E146", {"start": v(-13.94, 19.36) * mm, "end": v(-13.92, 19.59) * mm});
            skSolve(sketch);
        }
        {
            var Q0;
            Q0 = qSketchRegion(id + "F32", true);
            extrude(context, id + "F33", {"entities" : qUnion([Q0]), "operationType" : NewBodyOperationType.REMOVE, "oppositeDirection" : true, "depth" : 1.52 * mm, "offsetDistance" : 25.4 * mm});
        }
    });
